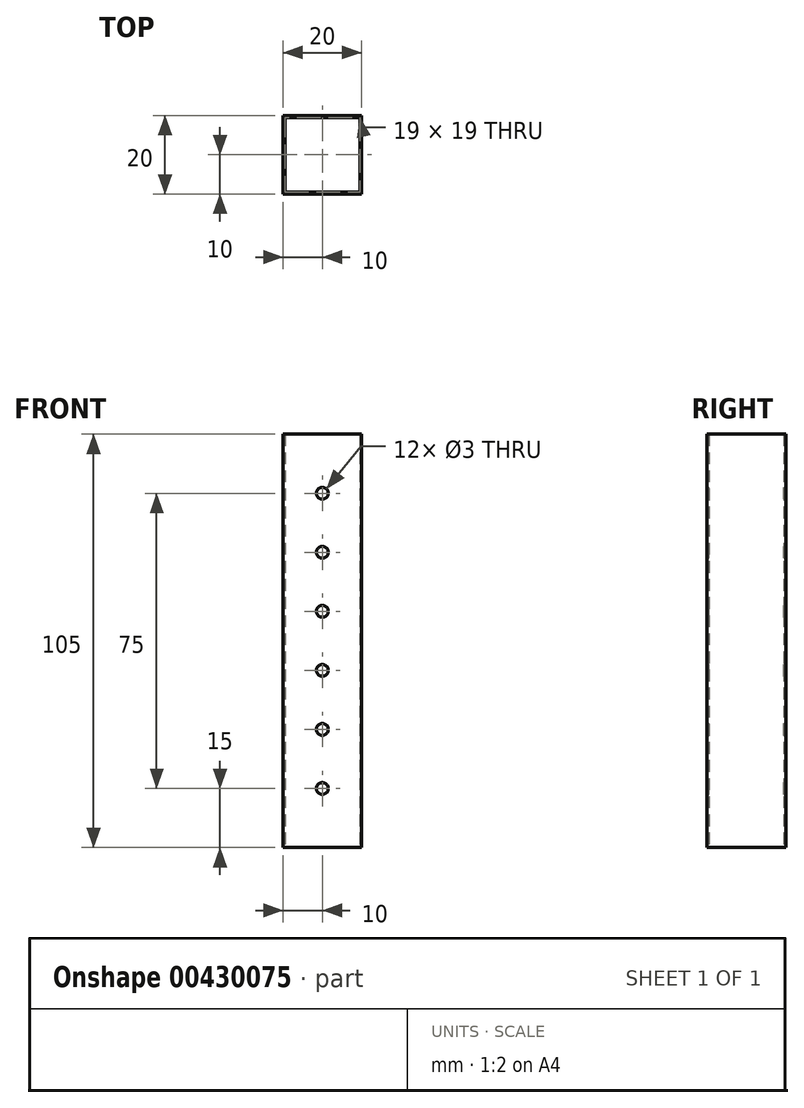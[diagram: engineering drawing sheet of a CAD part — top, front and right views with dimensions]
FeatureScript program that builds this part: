
annotation { "Feature Type Name" : "Feature", "Feature Type Description" : "" }
export const myFeature = defineFeature(function(context is Context, id is Id, definition is map)
    precondition{}
    {
        {
            var Q0;
            Q0=qCreatedBy(makeId("Top.planeOp"),FACE);
            var sketch = newSketch(context, id + "F0", { "sketchPlane" : qUnion([Q0])});
            skLineSegment(sketch, "E0.bottom", {"start": v(10, 10) * mm, "end": v(-10, 10) * mm});
            skLineSegment(sketch, "E0.top", {"start": v(10, -10) * mm, "end": v(-10, -10) * mm});
            skLineSegment(sketch, "E0.left", {"start": v(10, 10) * mm, "end": v(10, -10) * mm});
            skLineSegment(sketch, "E0.right", {"start": v(-10, 10) * mm, "end": v(-10, -10) * mm});
            skPoint(sketch, "E0.middle", {"position": v(0, 0) * mm});
            skLineSegment(sketch, "E1.bottom", {"start": v(9.5, 9.5) * mm, "end": v(-9.5, 9.5) * mm});
            skLineSegment(sketch, "E1.top", {"start": v(9.5, -9.5) * mm, "end": v(-9.5, -9.5) * mm});
            skLineSegment(sketch, "E1.left", {"start": v(9.5, 9.5) * mm, "end": v(9.5, -9.5) * mm});
            skLineSegment(sketch, "E1.right", {"start": v(-9.5, 9.5) * mm, "end": v(-9.5, -9.5) * mm});
            skSolve(sketch);
        }
        {
            var Q0;
            Q0 = qSketchRegion(id + "F0", true);
            extrude(context, id + "F1", {"entities" : qUnion([Q0]), "depth" : (15 * 7) * mm});
        }
        {
            var Q0;
            Q0=makeQuery(id+"F1.opExtrude","SWEPT_FACE",FACE,{"disambiguationData":[OSD([sQuery(id+"F0.wireOp",EDGE,"E0.bottom")])]});
            var sketch = newSketch(context, id + "F2", { "sketchPlane" : qUnion([Q0])});
            skCircle(sketch, "E2", {"center": v(0, 90) * mm, "radius": 1.5 * mm});
            skCircle(sketch, "E3", {"center": v(0, 75) * mm, "radius": 1.5 * mm});
            skCircle(sketch, "E4", {"center": v(0, 60) * mm, "radius": 1.5 * mm});
            skCircle(sketch, "E5", {"center": v(0, 45) * mm, "radius": 1.5 * mm});
            skCircle(sketch, "E6", {"center": v(0, 30) * mm, "radius": 1.5 * mm});
            skCircle(sketch, "E7", {"center": v(0, 15) * mm, "radius": 1.5 * mm});
            skSolve(sketch);
        }
        {
            var Q0;
            Q0=makeQuery(id+"F2.imprint","IMPRINT",FACE,{"disambiguationData":[TD([[makeQuery(id+"F2.imprint","IMPRINT",EDGE,{"derivedFrom":sQuery(id+"F2.wireOp",EDGE,"E2")}),1.0]])]});
            var Q1;
            Q1=makeQuery(id+"F2.imprint","IMPRINT",FACE,{"disambiguationData":[TD([[makeQuery(id+"F2.imprint","IMPRINT",EDGE,{"derivedFrom":sQuery(id+"F2.wireOp",EDGE,"E3")}),1.0]])]});
            var Q2;
            Q2=makeQuery(id+"F2.imprint","IMPRINT",FACE,{"disambiguationData":[TD([[makeQuery(id+"F2.imprint","IMPRINT",EDGE,{"derivedFrom":sQuery(id+"F2.wireOp",EDGE,"E4")}),1.0]])]});
            var Q3;
            Q3=makeQuery(id+"F2.imprint","IMPRINT",FACE,{"disambiguationData":[TD([[makeQuery(id+"F2.imprint","IMPRINT",EDGE,{"derivedFrom":sQuery(id+"F2.wireOp",EDGE,"E5")}),1.0]])]});
            var Q4;
            Q4=makeQuery(id+"F2.imprint","IMPRINT",FACE,{"disambiguationData":[TD([[makeQuery(id+"F2.imprint","IMPRINT",EDGE,{"derivedFrom":sQuery(id+"F2.wireOp",EDGE,"E6")}),1.0]])]});
            var Q5;
            Q5=makeQuery(id+"F2.imprint","IMPRINT",FACE,{"disambiguationData":[TD([[makeQuery(id+"F2.imprint","IMPRINT",EDGE,{"derivedFrom":sQuery(id+"F2.wireOp",EDGE,"E7")}),1.0]])]});
            extrude(context, id + "F3", {"entities" : qUnion([Q0, Q1, Q2, Q3, Q4, Q5]), "operationType" : NewBodyOperationType.REMOVE, "oppositeDirection" : true, "depth" : 25 * mm});
        }
    });
